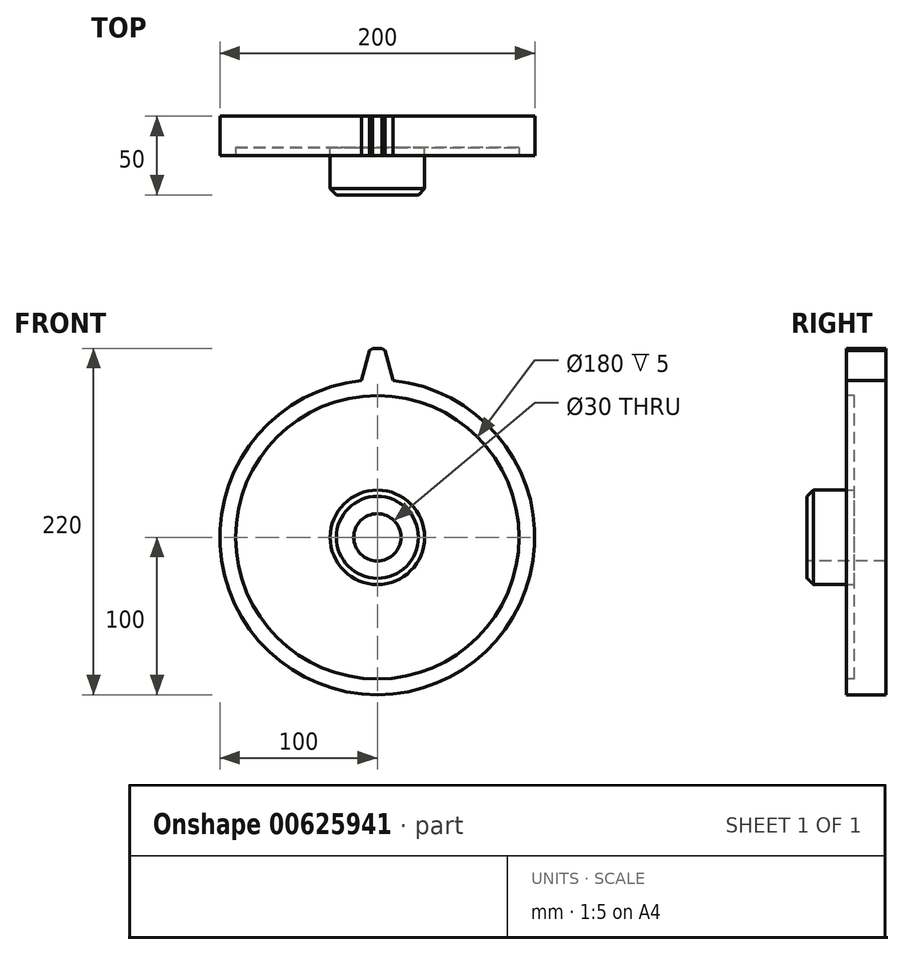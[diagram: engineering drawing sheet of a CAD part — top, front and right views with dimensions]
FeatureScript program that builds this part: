
annotation { "Feature Type Name" : "Feature", "Feature Type Description" : "" }
export const myFeature = defineFeature(function(context is Context, id is Id, definition is map)
    precondition{}
    {
        {
            var Q0;
            Q0=qCreatedBy(makeId("Front.planeOp"),FACE);
            var sketch = newSketch(context, id + "F0", { "sketchPlane" : qUnion([Q0])});
            skCircle(sketch, "E0", {"center": v(0, 0) * mm, "radius": 100 * mm});
            skSolve(sketch);
        }
        {
            var Q0;
            Q0=makeQuery(id+"F0.imprint","IMPRINT",FACE,{"disambiguationData":[TD([[makeQuery(id+"F0.imprint","IMPRINT",EDGE,{"derivedFrom":sQuery(id+"F0.wireOp",EDGE,"E0")}),1.0]])]});
            extrude(context, id + "F1", {"entities" : qUnion([Q0]), "depth" : 25 * mm, "offsetDistance" : 25 * mm});
        }
        {
            var Q0;
            Q0=qCreatedBy(makeId("Front.planeOp"),FACE);
            var sketch = newSketch(context, id + "F2", { "sketchPlane" : qUnion([Q0])});
            skLineSegment(sketch, "E1", {"start": v(-4.5, 120) * mm, "end": v(4.5, 120) * mm});
            skLineSegment(sketch, "E2", {"start": v(-10, 99.5) * mm, "end": v(10, 99.5) * mm});
            skLineSegment(sketch, "E3", {"start": v(-4.5, 120) * mm, "end": v(-10, 99.5) * mm});
            skLineSegment(sketch, "E4", {"start": v(4.5, 120) * mm, "end": v(10, 99.5) * mm});
            skSolve(sketch);
        }
        {
            var Q0;
            Q0=makeQuery(id+"F2.imprint","IMPRINT",FACE,{"disambiguationData":[TD([[makeQuery(id+"F2.imprint","IMPRINT",EDGE,{"derivedFrom":sQuery(id+"F2.wireOp",EDGE,"E1")}),-1.0]])]});
            extrude(context, id + "F3", {"entities" : qUnion([Q0]), "operationType" : NewBodyOperationType.ADD, "depth" : 25 * mm, "offsetDistance" : 25 * mm});
        }
        {
            var Q0;
            Q0=makeQuery(id+"F3.opExtrude","SWEPT_EDGE",EDGE,{"disambiguationData":[OSD([sQuery(id+"F2.wireOp",EDGE,"E1"),sQuery(id+"F2.wireOp",EDGE,"E4")])]});
            var Q1;
            Q1=makeQuery(id+"F3.opExtrude","SWEPT_EDGE",EDGE,{"disambiguationData":[OSD([sQuery(id+"F2.wireOp",EDGE,"E1"),sQuery(id+"F2.wireOp",EDGE,"E3")])]});
            chamfer(context, id + "F4", {"entities" : qUnion([Q0, Q1]), "width" : 2 * mm, "tangentPropagation" : true});
        }
        {
            var Q0;
            Q0=makeQuery(id+"F3.opExtrude","SWEPT_EDGE",EDGE,{"disambiguationData":[OSD([sQuery(id+"F2.wireOp",EDGE,"E2"),sQuery(id+"F2.wireOp",EDGE,"E4")])]});
            var Q1;
            Q1=makeQuery(id+"F3.opExtrude","SWEPT_EDGE",EDGE,{"disambiguationData":[OSD([sQuery(id+"F2.wireOp",EDGE,"E2"),sQuery(id+"F2.wireOp",EDGE,"E3")])]});
            fillet(context, id + "F5", {"entities" : qUnion([Q0, Q1]), "radius" : 5 * mm, "tangentPropagation" : true, "allowEdgeOverflow" : false});
        }
        {
            var Q0;
            {var subQ0=sQuery(id+"F2.wireOp",EDGE,"E4");var subQ1=sQuery(id+"F2.wireOp",EDGE,"E3");var subQ2=sQuery(id+"F2.wireOp",EDGE,"E2");var subQ3=sQuery(id+"F2.wireOp",EDGE,"E1");Q0=makeQuery(id+"FFdQa31eILTMau0_1.19.F3.boolean.opBoolean","MERGE",FACE,{"derivedFrom":[makeQuery(id+"FFdQa31eILTMau0_1.18.F3.boolean.opBoolean","MERGE",FACE,{"derivedFrom":[makeQuery(id+"FFdQa31eILTMau0_1.17.F3.boolean.opBoolean","MERGE",FACE,{"derivedFrom":[makeQuery(id+"FFdQa31eILTMau0_1.16.F3.boolean.opBoolean","MERGE",FACE,{"derivedFrom":[makeQuery(id+"FFdQa31eILTMau0_1.15.F3.boolean.opBoolean","MERGE",FACE,{"derivedFrom":[makeQuery(id+"FFdQa31eILTMau0_1.14.F3.boolean.opBoolean","MERGE",FACE,{"derivedFrom":[makeQuery(id+"FFdQa31eILTMau0_1.13.F3.boolean.opBoolean","MERGE",FACE,{"derivedFrom":[makeQuery(id+"FFdQa31eILTMau0_1.12.F3.boolean.opBoolean","MERGE",FACE,{"derivedFrom":[makeQuery(id+"FFdQa31eILTMau0_1.11.F3.boolean.opBoolean","MERGE",FACE,{"derivedFrom":[makeQuery(id+"FFdQa31eILTMau0_1.10.F3.boolean.opBoolean","MERGE",FACE,{"derivedFrom":[makeQuery(id+"FFdQa31eILTMau0_1.9.F3.boolean.opBoolean","MERGE",FACE,{"derivedFrom":[makeQuery(id+"FFdQa31eILTMau0_1.8.F3.boolean.opBoolean","MERGE",FACE,{"derivedFrom":[makeQuery(id+"FFdQa31eILTMau0_1.7.F3.boolean.opBoolean","MERGE",FACE,{"derivedFrom":[makeQuery(id+"FFdQa31eILTMau0_1.6.F3.boolean.opBoolean","MERGE",FACE,{"derivedFrom":[makeQuery(id+"FFdQa31eILTMau0_1.5.F3.boolean.opBoolean","MERGE",FACE,{"derivedFrom":[makeQuery(id+"FFdQa31eILTMau0_1.4.F3.boolean.opBoolean","MERGE",FACE,{"derivedFrom":[makeQuery(id+"FFdQa31eILTMau0_1.3.F3.boolean.opBoolean","MERGE",FACE,{"derivedFrom":[makeQuery(id+"FFdQa31eILTMau0_1.2.F3.boolean.opBoolean","MERGE",FACE,{"derivedFrom":[makeQuery(id+"FFdQa31eILTMau0_1.1.F3.boolean.opBoolean","MERGE",FACE,{"derivedFrom":[makeQuery(id+"F3.boolean.opBoolean","MERGE",FACE,{"derivedFrom":[makeQuery(id+"F1.opExtrude","CAP_FACE",FACE,{"disambiguationData":[OSD([sQuery(id+"F0.wireOp",EDGE,"E0")])],"isStart":false}),makeQuery(id+"F3.opExtrude","CAP_FACE",FACE,{"disambiguationData":[OSD([subQ3,subQ2,subQ1,subQ0])],"isStart":false})]}),makeQuery(id+"FFdQa31eILTMau0_1.1.F3.opExtrude","CAP_FACE",FACE,{"disambiguationData":[OSD([subQ3,subQ2,subQ1,subQ0])],"isStart":false})]}),makeQuery(id+"FFdQa31eILTMau0_1.2.F3.opExtrude","CAP_FACE",FACE,{"disambiguationData":[OSD([subQ3,subQ2,subQ1,subQ0])],"isStart":false})]}),makeQuery(id+"FFdQa31eILTMau0_1.3.F3.opExtrude","CAP_FACE",FACE,{"disambiguationData":[OSD([subQ3,subQ2,subQ1,subQ0])],"isStart":false})]}),makeQuery(id+"FFdQa31eILTMau0_1.4.F3.opExtrude","CAP_FACE",FACE,{"disambiguationData":[OSD([subQ3,subQ2,subQ1,subQ0])],"isStart":false})]}),makeQuery(id+"FFdQa31eILTMau0_1.5.F3.opExtrude","CAP_FACE",FACE,{"disambiguationData":[OSD([subQ3,subQ2,subQ1,subQ0])],"isStart":false})]}),makeQuery(id+"FFdQa31eILTMau0_1.6.F3.opExtrude","CAP_FACE",FACE,{"disambiguationData":[OSD([subQ3,subQ2,subQ1,subQ0])],"isStart":false})]}),makeQuery(id+"FFdQa31eILTMau0_1.7.F3.opExtrude","CAP_FACE",FACE,{"disambiguationData":[OSD([subQ3,subQ2,subQ1,subQ0])],"isStart":false})]}),makeQuery(id+"FFdQa31eILTMau0_1.8.F3.opExtrude","CAP_FACE",FACE,{"disambiguationData":[OSD([subQ3,subQ2,subQ1,subQ0])],"isStart":false})]}),makeQuery(id+"FFdQa31eILTMau0_1.9.F3.opExtrude","CAP_FACE",FACE,{"disambiguationData":[OSD([subQ3,subQ2,subQ1,subQ0])],"isStart":false})]}),makeQuery(id+"FFdQa31eILTMau0_1.10.F3.opExtrude","CAP_FACE",FACE,{"disambiguationData":[OSD([subQ3,subQ2,subQ1,subQ0])],"isStart":false})]}),makeQuery(id+"FFdQa31eILTMau0_1.11.F3.opExtrude","CAP_FACE",FACE,{"disambiguationData":[OSD([subQ3,subQ2,subQ1,subQ0])],"isStart":false})]}),makeQuery(id+"FFdQa31eILTMau0_1.12.F3.opExtrude","CAP_FACE",FACE,{"disambiguationData":[OSD([subQ3,subQ2,subQ1,subQ0])],"isStart":false})]}),makeQuery(id+"FFdQa31eILTMau0_1.13.F3.opExtrude","CAP_FACE",FACE,{"disambiguationData":[OSD([subQ3,subQ2,subQ1,subQ0])],"isStart":false})]}),makeQuery(id+"FFdQa31eILTMau0_1.14.F3.opExtrude","CAP_FACE",FACE,{"disambiguationData":[OSD([subQ3,subQ2,subQ1,subQ0])],"isStart":false})]}),makeQuery(id+"FFdQa31eILTMau0_1.15.F3.opExtrude","CAP_FACE",FACE,{"disambiguationData":[OSD([subQ3,subQ2,subQ1,subQ0])],"isStart":false})]}),makeQuery(id+"FFdQa31eILTMau0_1.16.F3.opExtrude","CAP_FACE",FACE,{"disambiguationData":[OSD([subQ3,subQ2,subQ1,subQ0])],"isStart":false})]}),makeQuery(id+"FFdQa31eILTMau0_1.17.F3.opExtrude","CAP_FACE",FACE,{"disambiguationData":[OSD([subQ3,subQ2,subQ1,subQ0])],"isStart":false})]}),makeQuery(id+"FFdQa31eILTMau0_1.18.F3.opExtrude","CAP_FACE",FACE,{"disambiguationData":[OSD([subQ3,subQ2,subQ1,subQ0])],"isStart":false})]}),makeQuery(id+"FFdQa31eILTMau0_1.19.F3.opExtrude","CAP_FACE",FACE,{"disambiguationData":[OSD([subQ3,subQ2,subQ1,subQ0])],"isStart":false})]});}
            var sketch = newSketch(context, id + "F6", { "sketchPlane" : qUnion([Q0])});
            skCircle(sketch, "E5", {"center": v(0, 0) * mm, "radius": 90 * mm});
            skSolve(sketch);
        }
        {
            var Q0;
            Q0=makeQuery(id+"F6.imprint","IMPRINT",FACE,{"disambiguationData":[TD([[makeQuery(id+"F6.imprint","IMPRINT",EDGE,{"derivedFrom":sQuery(id+"F6.wireOp",EDGE,"E5")}),1.0]])]});
            extrude(context, id + "F7", {"entities" : qUnion([Q0]), "operationType" : NewBodyOperationType.REMOVE, "oppositeDirection" : true, "depth" : 5 * mm, "offsetDistance" : 25 * mm});
        }
        {
            var Q0;
            Q0=makeQuery(id+"F7.boolean.opBoolean","COPY",FACE,{"derivedFrom":makeQuery(id+"F7.opExtrude","CAP_FACE",FACE,{"disambiguationData":[OSD([sQuery(id+"F6.wireOp",EDGE,"E5")])],"isStart":false})});
            var sketch = newSketch(context, id + "F8", { "sketchPlane" : qUnion([Q0])});
            skCircle(sketch, "E6", {"center": v(0, 0) * mm, "radius": 30 * mm});
            skSolve(sketch);
        }
        {
            var Q0;
            Q0=makeQuery(id+"F8.imprint","IMPRINT",FACE,{"disambiguationData":[TD([[makeQuery(id+"F8.imprint","IMPRINT",EDGE,{"derivedFrom":sQuery(id+"F8.wireOp",EDGE,"E6")}),1.0]])]});
            extrude(context, id + "F9", {"entities" : qUnion([Q0]), "operationType" : NewBodyOperationType.ADD, "depth" : 30 * mm, "offsetDistance" : 25 * mm});
        }
        {
            var Q0;
            Q0=makeQuery(id+"F9.opExtrude","CAP_FACE",FACE,{"disambiguationData":[OSD([sQuery(id+"F8.wireOp",EDGE,"E6")])],"isStart":false});
            var sketch = newSketch(context, id + "F10", { "sketchPlane" : qUnion([Q0])});
            skCircle(sketch, "E7", {"center": v(0, 0) * mm, "radius": 15 * mm});
            skSolve(sketch);
        }
        {
            var Q0;
            Q0=makeQuery(id+"F10.imprint","IMPRINT",FACE,{"disambiguationData":[TD([[makeQuery(id+"F10.imprint","IMPRINT",EDGE,{"derivedFrom":sQuery(id+"F10.wireOp",EDGE,"E7")}),1.0]])]});
            extrude(context, id + "F11", {"entities" : qUnion([Q0]), "operationType" : NewBodyOperationType.REMOVE, "endBound" : BoundingType.THROUGH_ALL, "oppositeDirection" : true, "depth" : 25 * mm, "offsetDistance" : 25 * mm});
        }
        {
            var Q0;
            Q0=makeQuery(id+"F9.opExtrude","CAP_EDGE",EDGE,{"disambiguationData":[OSD([sQuery(id+"F8.wireOp",EDGE,"E6")])],"isStart":false});
            var Q1;
            Q1=makeQuery(id+"F11.boolean.opBoolean","COPY",EDGE,{"derivedFrom":makeQuery(id+"F11.opExtrude","CAP_EDGE",EDGE,{"disambiguationData":[OSD([sQuery(id+"F10.wireOp",EDGE,"E7")])],"isStart":true})});
            chamfer(context, id + "F12", {"entities" : qUnion([Q0, Q1]), "width" : 4 * mm, "tangentPropagation" : true});
        }
    });
